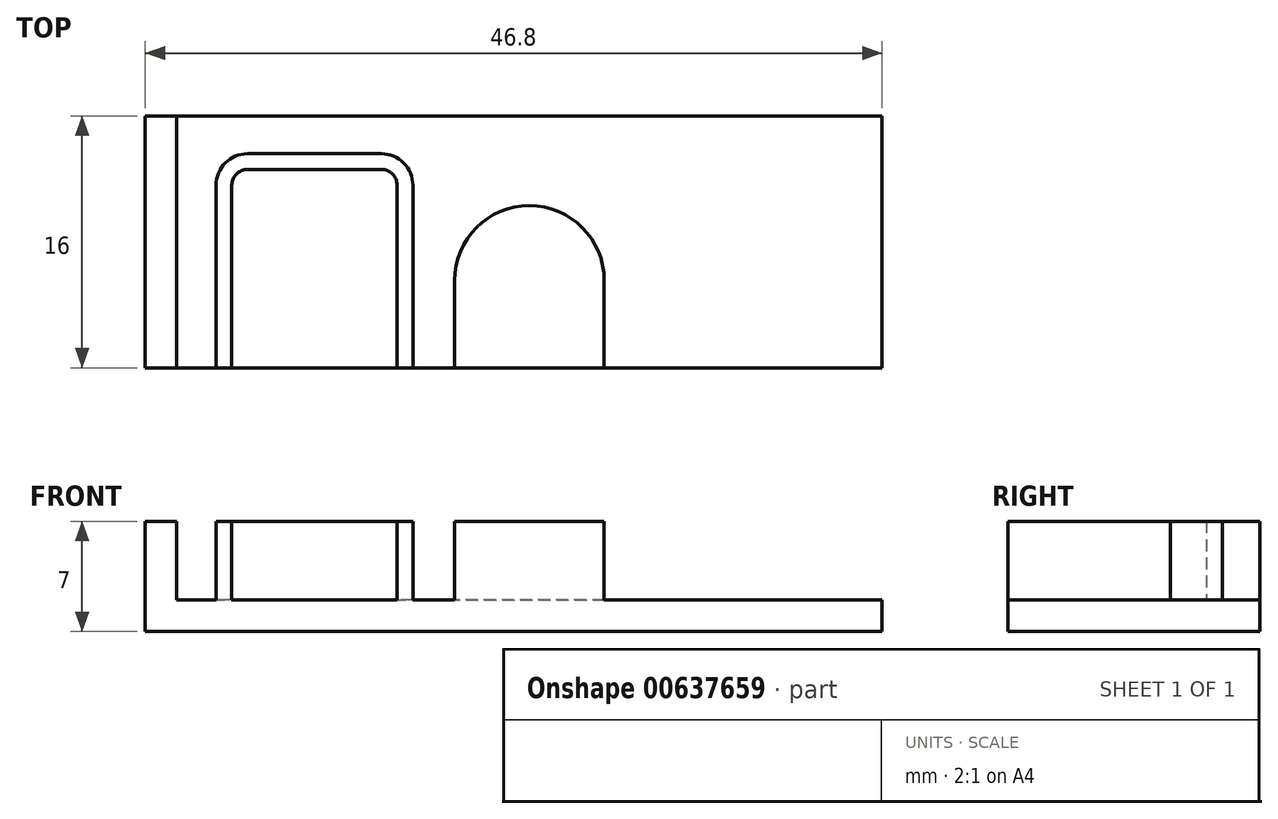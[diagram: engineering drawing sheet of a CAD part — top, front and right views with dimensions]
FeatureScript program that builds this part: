
annotation { "Feature Type Name" : "Feature", "Feature Type Description" : "" }
export const myFeature = defineFeature(function(context is Context, id is Id, definition is map)
    precondition{}
    {
        {
            var Q0;
            Q0=qCreatedBy(makeId("Top.planeOp"),FACE);
            var sketch = newSketch(context, id + "F0", { "sketchPlane" : qUnion([Q0])});
            skLineSegment(sketch, "E0.bottom", {"start": v(-22.4, -8) * mm, "end": v(22.4, -8) * mm});
            skLineSegment(sketch, "E0.top", {"start": v(-22.4, 8) * mm, "end": v(22.4, 8) * mm});
            skLineSegment(sketch, "E0.left", {"start": v(-22.4, -8) * mm, "end": v(-22.4, 8) * mm});
            skLineSegment(sketch, "E0.right", {"start": v(22.4, -8) * mm, "end": v(22.4, 8) * mm});
            skSolve(sketch);
        }
        {
            var Q0;
            Q0 = qSketchRegion(id + "F0", true);
            extrude(context, id + "F1", {"entities" : qUnion([Q0]), "depth" : 2 * mm, "offsetDistance" : 25 * mm});
        }
        {
            var Q0;
            Q0=makeQuery(id+"F1.opExtrude","CAP_FACE",FACE,{"disambiguationData":[OSD([sQuery(id+"F0.wireOp",EDGE,"E0.bottom"),sQuery(id+"F0.wireOp",EDGE,"E0.top"),sQuery(id+"F0.wireOp",EDGE,"E0.left"),sQuery(id+"F0.wireOp",EDGE,"E0.right")])],"isStart":false});
            var sketch = newSketch(context, id + "F2", { "sketchPlane" : qUnion([Q0])});
            skLineSegment(sketch, "E1.0", {"start": v(-22.4, -8) * mm, "end": v(22.4, -8) * mm, "construction": true});
            skLineSegment(sketch, "E1.1", {"start": v(-22.4, -8) * mm, "end": v(-22.4, 8) * mm, "construction": true});
            skLineSegment(sketch, "E2", {"start": v(-19.9, -8) * mm, "end": v(-19.9, 3.6) * mm});
            skLineSegment(sketch, "E3", {"start": v(-17.9, 5.6) * mm, "end": v(-9.4, 5.6) * mm});
            skLineSegment(sketch, "E4", {"start": v(-7.4, 3.6) * mm, "end": v(-7.4, -8) * mm});
            skLineSegment(sketch, "E5.0", {"start": v(-8.4, 3.6) * mm, "end": v(-8.4, -8) * mm});
            skLineSegment(sketch, "E5.1", {"start": v(-17.9, 4.6) * mm, "end": v(-9.4, 4.6) * mm});
            skLineSegment(sketch, "E5.2", {"start": v(-18.9, -8) * mm, "end": v(-18.9, 3.6) * mm});
            skLineSegment(sketch, "E6", {"start": v(-19.9, -8) * mm, "end": v(-18.9, -8) * mm});
            skLineSegment(sketch, "E7", {"start": v(-8.4, -8) * mm, "end": v(-7.4, -8) * mm});
            skPoint(sketch, "E8.visualSharp", {"position": v(-18.9, 4.6) * mm});
            skArc(sketch, "E8.filletArc", {"start": v(-17.9, 4.6) * mm, "mid": v(-18.6, 4.3) * mm, "end": v(-18.9, 3.6) * mm});
            skPoint(sketch, "E9.visualSharp", {"position": v(-8.4, 4.6) * mm});
            skArc(sketch, "E9.filletArc", {"start": v(-8.4, 3.6) * mm, "mid": v(-8.7, 4.3) * mm, "end": v(-9.4, 4.6) * mm});
            skPoint(sketch, "E10.visualSharp", {"position": v(-19.9, 5.6) * mm});
            skArc(sketch, "E10.filletArc", {"start": v(-17.9, 5.6) * mm, "mid": v(-19.31, 5.01) * mm, "end": v(-19.9, 3.6) * mm});
            skPoint(sketch, "E11.visualSharp", {"position": v(-7.4, 5.6) * mm});
            skArc(sketch, "E11.filletArc", {"start": v(-7.4, 3.6) * mm, "mid": v(-7.99, 5.01) * mm, "end": v(-9.4, 5.6) * mm});
            skSolve(sketch);
        }
        {
            var Q0;
            {var subQ3=sQuery(id+"F2.wireOp",EDGE,"E2");Q0=makeQuery(id+"F2.imprint","IMPRINT",FACE,{"disambiguationData":[TD([[makeQuery(id+"F2.imprint","IMPRINT",EDGE,{"derivedFrom":subQ3}),1.0]])]});}
            var sketch = newSketch(context, id + "F3", { "sketchPlane" : qUnion([Q0])});
            skArc(sketch, "E12", {"start": v(4.75, -2.45) * mm, "mid": v(0, 2.3) * mm, "end": v(-4.75, -2.45) * mm});
            skLineSegment(sketch, "E13.0", {"start": v(-22.4, -8) * mm, "end": v(22.4, -8) * mm, "construction": true});
            skLineSegment(sketch, "E14", {"start": v(-4.75, -8) * mm, "end": v(-4.75, -2.45) * mm});
            skLineSegment(sketch, "E15.MirrorCS", {"start": v(4.75, -8) * mm, "end": v(4.75, -2.45) * mm});
            skLineSegment(sketch, "E16", {"start": v(-4.75, -8) * mm, "end": v(4.75, -8) * mm});
            skSolve(sketch);
        }
        {
            var Q0;
            Q0=makeQuery(id+"F2.imprint","IMPRINT",FACE,{"disambiguationData":[TD([[makeQuery(id+"F2.imprint","IMPRINT",EDGE,{"derivedFrom":sQuery(id+"F2.wireOp",EDGE,"E2")}),-1.0]])]});
            extrude(context, id + "F4", {"entities" : qUnion([Q0]), "operationType" : NewBodyOperationType.ADD, "depth" : 5 * mm, "offsetDistance" : 25 * mm});
        }
        {
            var Q0;
            Q0=makeQuery(id+"F3.imprint","IMPRINT",FACE,{"disambiguationData":[TD([[makeQuery(id+"F3.imprint","IMPRINT",EDGE,{"derivedFrom":sQuery(id+"F3.wireOp",EDGE,"E12")}),1.0]])]});
            extrude(context, id + "F5", {"entities" : qUnion([Q0]), "operationType" : NewBodyOperationType.ADD, "depth" : 5 * mm, "offsetDistance" : 25 * mm});
        }
        {
            var Q0;
            Q0=qCreatedBy(makeId("Top.planeOp"),FACE);
            var sketch = newSketch(context, id + "F6", { "sketchPlane" : qUnion([Q0])});
            skLineSegment(sketch, "E17.0", {"start": v(-22.4, -8) * mm, "end": v(-22.4, 8) * mm});
            skLineSegment(sketch, "E18", {"start": v(-22.4, -8) * mm, "end": v(-24.4, -8) * mm});
            skLineSegment(sketch, "E19", {"start": v(-24.4, -8) * mm, "end": v(-24.4, 8) * mm});
            skLineSegment(sketch, "E20", {"start": v(-24.4, 8) * mm, "end": v(-22.4, 8) * mm});
            skSolve(sketch);
        }
        {
            var Q0;
            Q0=makeQuery(id+"F6.imprint","IMPRINT",FACE,{"disambiguationData":[TD([[makeQuery(id+"F6.imprint","IMPRINT",EDGE,{"derivedFrom":sQuery(id+"F6.wireOp",EDGE,"E17.0")}),1.0]])]});
            var Q1;
            Q1=makeQuery(id+"F4.opExtrude","CAP_FACE",FACE,{"disambiguationData":[OSD([sQuery(id+"F2.wireOp",EDGE,"E2"),sQuery(id+"F2.wireOp",EDGE,"E3"),sQuery(id+"F2.wireOp",EDGE,"E4"),sQuery(id+"F2.wireOp",EDGE,"E5.0"),sQuery(id+"F2.wireOp",EDGE,"E5.1"),sQuery(id+"F2.wireOp",EDGE,"E5.2"),sQuery(id+"F2.wireOp",EDGE,"E6"),sQuery(id+"F2.wireOp",EDGE,"E7"),sQuery(id+"F2.wireOp",EDGE,"E8.filletArc"),sQuery(id+"F2.wireOp",EDGE,"E9.filletArc"),sQuery(id+"F2.wireOp",EDGE,"E10.filletArc"),sQuery(id+"F2.wireOp",EDGE,"E11.filletArc")])],"isStart":false});
            extrude(context, id + "F7", {"entities" : qUnion([Q0]), "operationType" : NewBodyOperationType.ADD, "endBound" : BoundingType.UP_TO_SURFACE, "depth" : 25 * mm, "endBoundEntityFace" : qUnion([Q1]), "offsetDistance" : 25 * mm});
        }
    });
